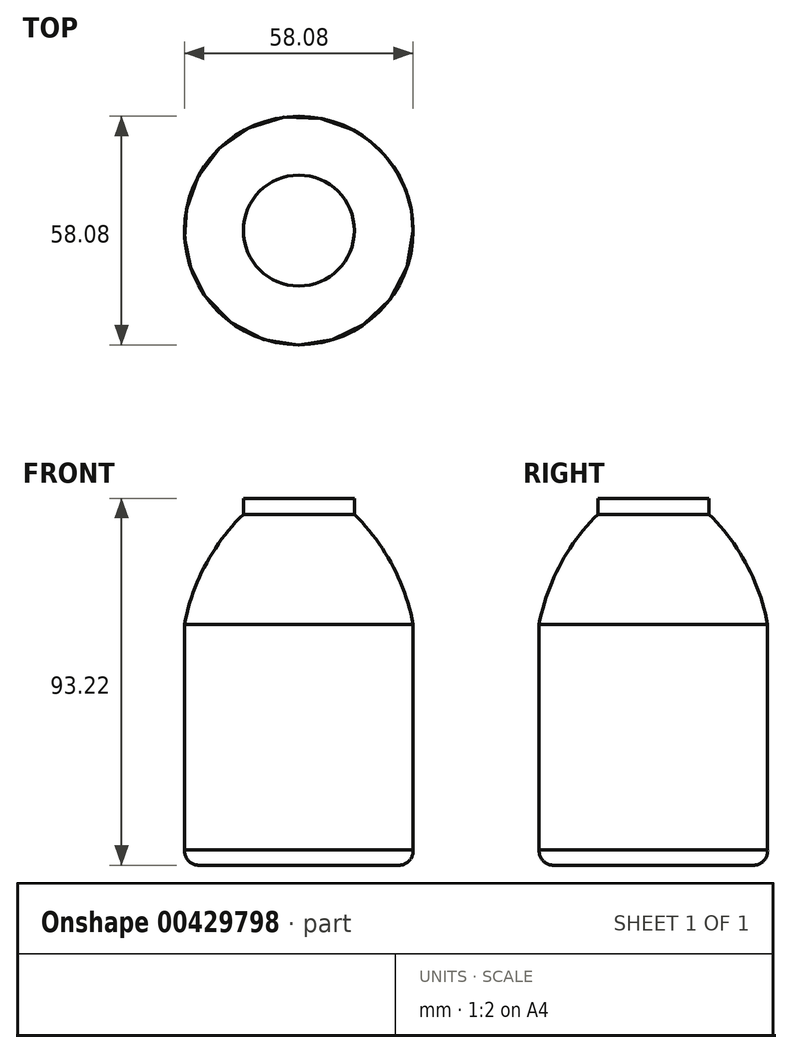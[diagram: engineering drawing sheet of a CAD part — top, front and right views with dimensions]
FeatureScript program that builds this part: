
annotation { "Feature Type Name" : "Feature", "Feature Type Description" : "" }
export const myFeature = defineFeature(function(context is Context, id is Id, definition is map)
    precondition{}
    {
        {
            var Q0;
            Q0=qCreatedBy(makeId("Front.planeOp"),FACE);
            var sketch = newSketch(context, id + "F0", { "sketchPlane" : qUnion([Q0])});
            skLineSegment(sketch, "E0", {"start": v(0, 0) * mm, "end": v(-25.4, 0) * mm});
            skArc(sketch, "E1", {"start": v(-29.03, 3.88) * mm, "mid": v(-28.06, 1.15) * mm, "end": v(-25.4, 0) * mm});
            skFitSpline(sketch, "E2", {"points": [v(-29.03, 3.88) * mm, v(-29.03, 61.21) * mm], "startDerivative": vector(0, 57.33) * mm, "endDerivative": vector(0, 57.33) * mm});
            skArc(sketch, "E3", {"start": v(-14.1, 89.17) * mm, "mid": v(-23.7, 76.33) * mm, "end": v(-29.03, 61.21) * mm});
            skLineSegment(sketch, "E4", {"start": v(-14.1, 89.17) * mm, "end": v(-14.1, 93.22) * mm});
            skLineSegment(sketch, "E5", {"start": v(-14.1, 93.22) * mm, "end": v(0, 93.22) * mm});
            skLineSegment(sketch, "E6", {"start": v(0, 93.22) * mm, "end": v(0, 0) * mm});
            skSolve(sketch);
        }
        {
            var Q0;
            Q0=makeQuery(id+"F0.imprint","IMPRINT",FACE,{"disambiguationData":[TD([[makeQuery(id+"F0.imprint","IMPRINT",EDGE,{"derivedFrom":sQuery(id+"F0.wireOp",EDGE,"E0")}),-1.0]])]});
            var Q1;
            Q1=sQuery(id+"F0.wireOp",EDGE,"E6");
            revolve(context, id + "F1", {"entities" : qUnion([Q0]), "axis" : qUnion([Q1]), "revolveType" : RevolveType.FULL});
        }
    });
